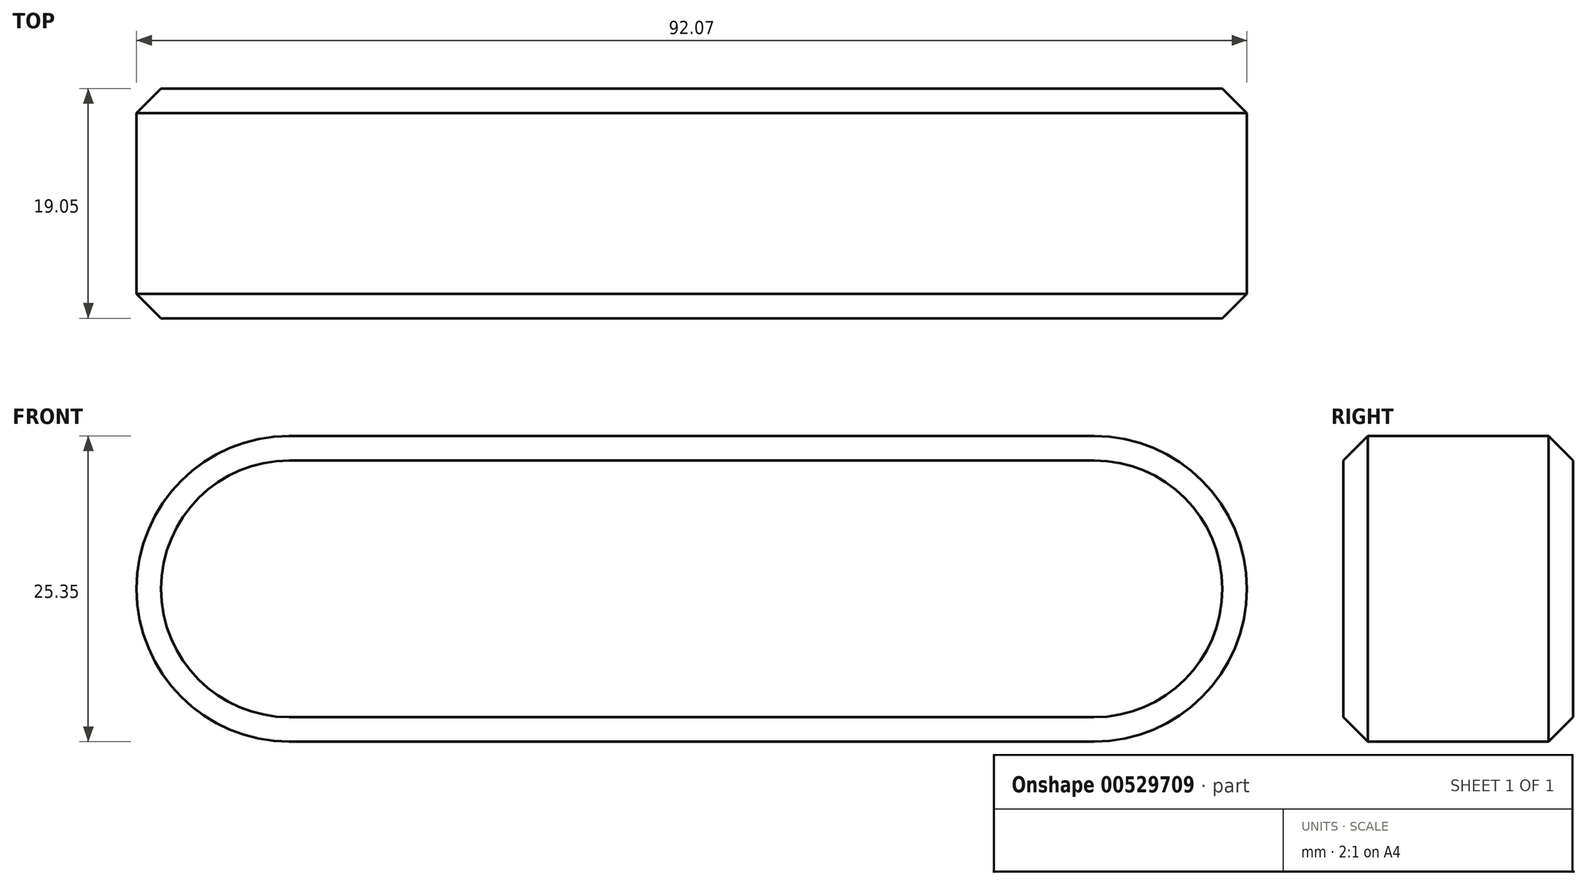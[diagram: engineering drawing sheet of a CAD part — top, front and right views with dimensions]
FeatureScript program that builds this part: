
annotation { "Feature Type Name" : "Feature", "Feature Type Description" : "" }
export const myFeature = defineFeature(function(context is Context, id is Id, definition is map)
    precondition{}
    {
        {
            var Q0;
            Q0=qCreatedBy(makeId("Front.planeOp"),FACE);
            var sketch = newSketch(context, id + "F0", { "sketchPlane" : qUnion([Q0])});
            skLineSegment(sketch, "E0.bottom", {"start": v(0, 0) * mm, "end": v(66.73, 0) * mm});
            skLineSegment(sketch, "E0.top", {"start": v(0, 25.35) * mm, "end": v(66.73, 25.35) * mm});
            skLineSegment(sketch, "E0.left", {"start": v(0, 0) * mm, "end": v(0, 25.35) * mm});
            skLineSegment(sketch, "E0.right", {"start": v(66.73, 0) * mm, "end": v(66.73, 25.35) * mm});
            skLineSegment(sketch, "E1", {"start": v(0, 12.67) * mm, "end": v(66.73, 12.67) * mm});
            skArc(sketch, "E2", {"start": v(0, 25.35) * mm, "mid": v(-12.67, 12.67) * mm, "end": v(0, 0) * mm});
            skArc(sketch, "E3", {"start": v(66.73, 0) * mm, "mid": v(79.4, 12.67) * mm, "end": v(66.73, 25.35) * mm});
            skSolve(sketch);
        }
        {
            var Q0;
            {var subQ0=sQuery(id+"F0.wireOp",EDGE,"E2");Q0=makeQuery(id+"F0.imprint","IMPRINT",FACE,{"disambiguationData":[TD([[makeQuery(id+"F0.imprint","IMPRINT",EDGE,{"derivedFrom":subQ0}),1.0]])]});}
            var Q1;
            {var subQ0=sQuery(id+"F0.wireOp",EDGE,"E0.top");Q1=makeQuery(id+"F0.imprint","IMPRINT",FACE,{"disambiguationData":[TD([[makeQuery(id+"F0.imprint","IMPRINT",EDGE,{"derivedFrom":subQ0}),-1.0]])]});}
            var Q2;
            {var subQ0=sQuery(id+"F0.wireOp",EDGE,"E0.bottom");Q2=makeQuery(id+"F0.imprint","IMPRINT",FACE,{"disambiguationData":[TD([[makeQuery(id+"F0.imprint","IMPRINT",EDGE,{"derivedFrom":subQ0}),1.0]])]});}
            var Q3;
            {var subQ0=sQuery(id+"F0.wireOp",EDGE,"E3");Q3=makeQuery(id+"F0.imprint","IMPRINT",FACE,{"disambiguationData":[TD([[makeQuery(id+"F0.imprint","IMPRINT",EDGE,{"derivedFrom":subQ0}),1.0]])]});}
            extrude(context, id + "F1", {"entities" : qUnion([Q0, Q1, Q2, Q3]), "depth" : 19.05 * mm, "offsetDistance" : 25.4 * mm});
        }
        {
            var Q0;
            Q0=makeQuery(id+"F1.opExtrude","CAP_FACE",FACE,{"disambiguationData":[OSD([sQuery(id+"F0.wireOp",EDGE,"E0.bottom"),sQuery(id+"F0.wireOp",EDGE,"E0.top"),sQuery(id+"F0.wireOp",EDGE,"E2"),sQuery(id+"F0.wireOp",EDGE,"E3")])],"isStart":true});
            chamfer(context, id + "F2", {"entities" : qUnion([Q0]), "width" : 2.03 * mm, "tangentPropagation" : true});
        }
        {
            var Q0;
            Q0=makeQuery(id+"F1.opExtrude","CAP_FACE",FACE,{"disambiguationData":[OSD([sQuery(id+"F0.wireOp",EDGE,"E0.bottom"),sQuery(id+"F0.wireOp",EDGE,"E0.top"),sQuery(id+"F0.wireOp",EDGE,"E2"),sQuery(id+"F0.wireOp",EDGE,"E3")])],"isStart":false});
            chamfer(context, id + "F3", {"entities" : qUnion([Q0]), "width" : 2.03 * mm, "tangentPropagation" : true});
        }
    });
